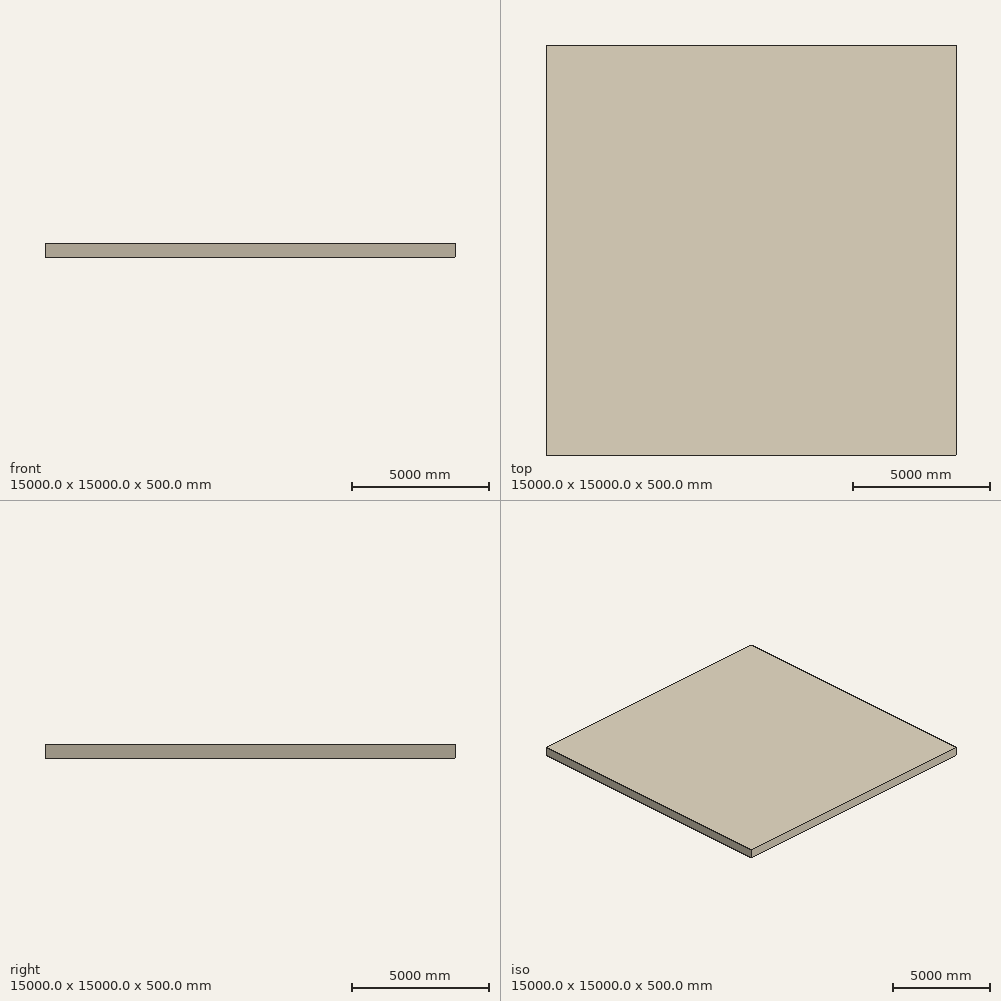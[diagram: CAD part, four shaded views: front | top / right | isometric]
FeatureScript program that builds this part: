
annotation { "Feature Type Name" : "Feature", "Feature Type Description" : "" }
export const myFeature = defineFeature(function(context is Context, id is Id, definition is map)
    precondition{}
    {
        {
            var Q0;
            Q0=qCreatedBy(makeId("Top.planeOp"),FACE);
            var sketch = newSketch(context, id + "F0", { "sketchPlane" : qUnion([Q0])});
            skLineSegment(sketch, "E0.bottom", {"start": v(-8757.58, 9378.73) * mm, "end": v(6242.42, 9378.73) * mm});
            skLineSegment(sketch, "E0.top", {"start": v(-8757.58, -5621.27) * mm, "end": v(6242.42, -5621.27) * mm});
            skLineSegment(sketch, "E0.left", {"start": v(-8757.58, 9378.73) * mm, "end": v(-8757.58, -5621.27) * mm});
            skLineSegment(sketch, "E0.right", {"start": v(6242.42, 9378.73) * mm, "end": v(6242.42, -5621.27) * mm});
            skSolve(sketch);
        }
        {
            var Q0;
            Q0 = qSketchRegion(id + "F0", true);
            extrude(context, id + "F1", {"entities" : qUnion([Q0]), "oppositeDirection" : true, "depth" : 500 * mm});
        }
    });
